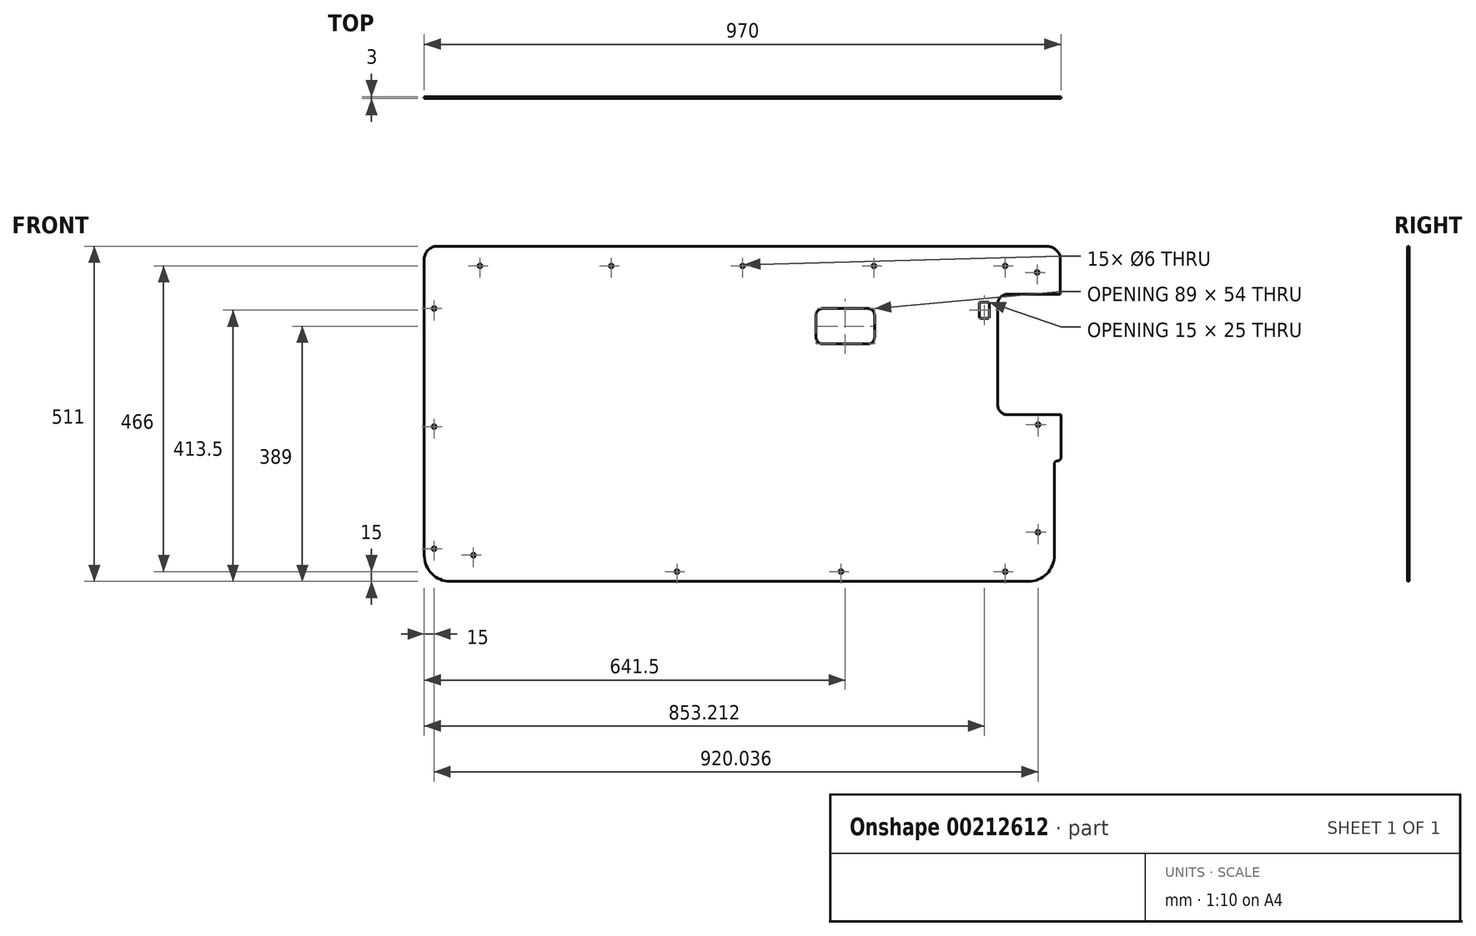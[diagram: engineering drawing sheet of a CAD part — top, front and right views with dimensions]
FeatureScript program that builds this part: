
annotation { "Feature Type Name" : "Feature", "Feature Type Description" : "" }
export const myFeature = defineFeature(function(context is Context, id is Id, definition is map)
    precondition{}
    {
        {
            var Q0;
            Q0=qCreatedBy(makeId("Front.planeOp"),FACE);
            var sketch = newSketch(context, id + "F0", { "sketchPlane" : qUnion([Q0])});
            skLineSegment(sketch, "E0.bottom", {"start": v(462.4, 255.5) * mm, "end": v(-465, 255.5) * mm});
            skLineSegment(sketch, "E0.top", {"start": v(435, -255.5) * mm, "end": v(435, -255.5) * mm});
            skLineSegment(sketch, "E0.right", {"start": v(-485, 235.5) * mm, "end": v(-485, -215.5) * mm});
            skPoint(sketch, "E0.middle", {"position": v(0, 0) * mm});
            skLineSegment(sketch, "E1", {"start": v(0, 509.33) * mm, "end": v(0, -613.63) * mm, "construction": true});
            skLineSegment(sketch, "E2", {"start": v(-633.66, 0) * mm, "end": v(624.03, 0) * mm, "construction": true});
            skPoint(sketch, "E2.endSnap0", {"position": v(457.9, 0) * mm});
            skPoint(sketch, "E3.visualSharp", {"position": v(-485, 255.5) * mm});
            skPoint(sketch, "E4.visualSharp", {"position": v(485, 255.5) * mm});
            skArc(sketch, "E4.filletArc", {"start": v(483.71, 240.43) * mm, "mid": v(475.46, 251.35) * mm, "end": v(462.4, 255.5) * mm});
            skPoint(sketch, "E5.visualSharp", {"position": v(-485, -255.5) * mm});
            skPoint(sketch, "E6.center.orphan", {"position": v(-400, 225.5) * mm});
            skArc(sketch, "E7.filletArc", {"start": v(-485, -215.5) * mm, "mid": v(-473.28, -243.78) * mm, "end": v(-445, -255.5) * mm});
            skArc(sketch, "E8.filletArc", {"start": v(-465, 255.5) * mm, "mid": v(-479.14, 249.64) * mm, "end": v(-485, 235.5) * mm});
            skLineSegment(sketch, "E9", {"start": v(457.9, 0) * mm, "end": v(457.9, 0) * mm});
            skLineSegment(sketch, "E10", {"start": v(483.71, 240.43) * mm, "end": v(483.71, 182.5) * mm});
            skLineSegment(sketch, "E11", {"start": v(388.71, 167.5) * mm, "end": v(388.71, 13.5) * mm});
            skLineSegment(sketch, "E12", {"start": v(112, 150.5) * mm, "end": v(112, 116.5) * mm});
            skLineSegment(sketch, "E13", {"start": v(122, 106.5) * mm, "end": v(191, 106.5) * mm});
            skLineSegment(sketch, "E14", {"start": v(201, 116.5) * mm, "end": v(201, 150.5) * mm});
            skLineSegment(sketch, "E15", {"start": v(122, 160.5) * mm, "end": v(191, 160.5) * mm});
            skPoint(sketch, "E16.visualSharp", {"position": v(112, 160.5) * mm});
            skArc(sketch, "E16.filletArc", {"start": v(122, 160.5) * mm, "mid": v(114.93, 157.57) * mm, "end": v(112, 150.5) * mm});
            skPoint(sketch, "E17.visualSharp", {"position": v(201, 160.5) * mm});
            skArc(sketch, "E17.filletArc", {"start": v(201, 150.5) * mm, "mid": v(198.07, 157.57) * mm, "end": v(191, 160.5) * mm});
            skPoint(sketch, "E18.visualSharp", {"position": v(201, 106.5) * mm});
            skArc(sketch, "E18.filletArc", {"start": v(191, 106.5) * mm, "mid": v(198.07, 109.43) * mm, "end": v(201, 116.5) * mm});
            skPoint(sketch, "E19.visualSharp", {"position": v(112, 106.5) * mm});
            skArc(sketch, "E19.filletArc", {"start": v(112, 116.5) * mm, "mid": v(114.93, 109.43) * mm, "end": v(122, 106.5) * mm});
            skLineSegment(sketch, "E20", {"start": v(360.71, 168.5) * mm, "end": v(360.71, 147.5) * mm});
            skLineSegment(sketch, "E21", {"start": v(362.71, 145.5) * mm, "end": v(373.71, 145.5) * mm});
            skLineSegment(sketch, "E22", {"start": v(375.71, 147.5) * mm, "end": v(375.71, 168.5) * mm});
            skLineSegment(sketch, "E23", {"start": v(373.71, 170.5) * mm, "end": v(362.71, 170.5) * mm});
            skPoint(sketch, "E24.visualSharp", {"position": v(360.71, 170.5) * mm});
            skArc(sketch, "E24.filletArc", {"start": v(362.71, 170.5) * mm, "mid": v(361.3, 169.91) * mm, "end": v(360.71, 168.5) * mm});
            skPoint(sketch, "E25.visualSharp", {"position": v(375.71, 170.5) * mm});
            skArc(sketch, "E25.filletArc", {"start": v(375.71, 168.5) * mm, "mid": v(375.13, 169.91) * mm, "end": v(373.71, 170.5) * mm});
            skPoint(sketch, "E26.visualSharp", {"position": v(375.71, 145.5) * mm});
            skArc(sketch, "E26.filletArc", {"start": v(373.71, 145.5) * mm, "mid": v(375.13, 146.09) * mm, "end": v(375.71, 147.5) * mm});
            skPoint(sketch, "E27.visualSharp", {"position": v(360.71, 145.5) * mm});
            skArc(sketch, "E27.filletArc", {"start": v(360.71, 147.5) * mm, "mid": v(361.3, 146.09) * mm, "end": v(362.71, 145.5) * mm});
            skPoint(sketch, "E28.center.orphan", {"position": v(-200, 225.5) * mm});
            skPoint(sketch, "E29.center.orphan", {"position": v(0, 225.5) * mm});
            skPoint(sketch, "E30.center.orphan", {"position": v(200, 225.5) * mm});
            skPoint(sketch, "E31.center.orphan", {"position": v(400, 225.5) * mm});
            skLineSegment(sketch, "E32", {"start": v(483.71, 182.5) * mm, "end": v(403.71, 182.5) * mm});
            skLineSegment(sketch, "E33", {"start": v(475, -215.5) * mm, "end": v(475, -81.5) * mm});
            skLineSegment(sketch, "E34", {"start": v(403.71, -1.5) * mm, "end": v(462.82, -1.5) * mm});
            skLineSegment(sketch, "E35", {"start": v(485, -1.5) * mm, "end": v(485, -61.5) * mm});
            skPoint(sketch, "E36.visualSharp", {"position": v(475, -71.5) * mm});
            skPoint(sketch, "E37.visualSharp", {"position": v(485, -1.5) * mm});
            skLineSegment(sketch, "E38", {"start": v(403.71, -1.5) * mm, "end": v(485, -1.5) * mm});
            skPoint(sketch, "E39.center.orphan", {"position": v(448.71, 215.5) * mm});
            skPoint(sketch, "E40.center.orphan", {"position": v(450, -16.5) * mm});
            skPoint(sketch, "E41.center.orphan", {"position": v(450, -180.5) * mm});
            skPoint(sketch, "E42.center.orphan", {"position": v(400, -240.5) * mm});
            skPoint(sketch, "E43.center.orphan", {"position": v(150, -240.5) * mm});
            skPoint(sketch, "E44.center.orphan", {"position": v(-100, -240.5) * mm});
            skPoint(sketch, "E45.center.orphan", {"position": v(-410, -215.5) * mm});
            skPoint(sketch, "E46.center.orphan", {"position": v(-470, -205.5) * mm});
            skPoint(sketch, "E47.center.orphan", {"position": v(-470, -19.5) * mm});
            skPoint(sketch, "E48.center.orphan", {"position": v(-470, 160.5) * mm});
            skPoint(sketch, "E49.visualSharp", {"position": v(388.71, 182.5) * mm});
            skArc(sketch, "E49.filletArc", {"start": v(403.71, 182.5) * mm, "mid": v(393.1, 178.1) * mm, "end": v(388.71, 167.5) * mm});
            skPoint(sketch, "E50.visualSharp", {"position": v(388.71, -1.5) * mm});
            skArc(sketch, "E50.filletArc", {"start": v(388.71, 13.5) * mm, "mid": v(393.1, 2.9) * mm, "end": v(403.71, -1.5) * mm});
            skLineSegment(sketch, "E51.trimOffspring", {"start": v(0, -255.5) * mm, "end": v(-445, -255.5) * mm});
            skPoint(sketch, "E52.visualSharp", {"position": v(475, -255.5) * mm});
            skArc(sketch, "E52.filletArc", {"start": v(435, -255.5) * mm, "mid": v(463.28, -243.78) * mm, "end": v(475, -215.5) * mm});
            skCircle(sketch, "E53", {"center": v(200.04, 225.5) * mm, "radius": 3 * mm});
            skPoint(sketch, "E54.center.orphan", {"position": v(399.93, 225.48) * mm});
            skCircle(sketch, "E55", {"center": v(399.97, 225.48) * mm, "radius": 3 * mm});
            skPoint(sketch, "E56.center.orphan", {"position": v(448.72, 215.5) * mm});
            skCircle(sketch, "E57", {"center": v(448.76, 215.5) * mm, "radius": 3 * mm});
            skCircle(sketch, "E58", {"center": v(450.04, -16.5) * mm, "radius": 3 * mm});
            skCircle(sketch, "E59", {"center": v(450, -180.5) * mm, "radius": 3 * mm});
            skCircle(sketch, "E60", {"center": v(400, -240.5) * mm, "radius": 3 * mm});
            skCircle(sketch, "E61", {"center": v(150, -240.5) * mm, "radius": 3 * mm});
            skCircle(sketch, "E62", {"center": v(-100, -240.5) * mm, "radius": 3 * mm});
            skCircle(sketch, "E63", {"center": v(-410, -215.5) * mm, "radius": 3 * mm});
            skCircle(sketch, "E64", {"center": v(-470, -205.5) * mm, "radius": 3 * mm});
            skCircle(sketch, "E65", {"center": v(-470, -19.5) * mm, "radius": 3 * mm});
            skCircle(sketch, "E66", {"center": v(-470, 160.5) * mm, "radius": 3 * mm});
            skCircle(sketch, "E67", {"center": v(-400, 225.5) * mm, "radius": 3 * mm});
            skCircle(sketch, "E68", {"center": v(-200, 225.5) * mm, "radius": 3 * mm});
            skCircle(sketch, "E69", {"center": v(0, 225.5) * mm, "radius": 3 * mm});
            skLineSegment(sketch, "E70", {"start": v(435, -255.5) * mm, "end": v(0, -255.5) * mm});
            skPoint(sketch, "E71.1.internal.orphan", {"position": v(480, -71.5) * mm});
            skPoint(sketch, "E71.startDerivative.orphan", {"position": v(485, -71.5) * mm});
            skLineSegment(sketch, "E72", {"start": v(480, -71.5) * mm, "end": v(480, -71.5) * mm});
            skLineSegment(sketch, "E73", {"start": v(475, -81.5) * mm, "end": v(475, -76.5) * mm});
            skArc(sketch, "E74.filletArc", {"start": v(480, -71.5) * mm, "mid": v(483.54, -70.04) * mm, "end": v(485, -66.5) * mm});
            skArc(sketch, "E75.filletArc", {"start": v(480, -71.5) * mm, "mid": v(476.46, -72.96) * mm, "end": v(475, -76.5) * mm});
            skLineSegment(sketch, "E76", {"start": v(485, -66.5) * mm, "end": v(485, -61.5) * mm});
            skSolve(sketch);
        }
        {
            var Q0;
            Q0=makeQuery(id+"F0.imprint","IMPRINT",FACE,{"disambiguationData":[TD([[makeQuery(id+"F0.imprint","IMPRINT",EDGE,{"derivedFrom":sQuery(id+"F0.wireOp",EDGE,"E0.bottom")}),1.0]])]});
            extrude(context, id + "F1", {"entities" : qUnion([Q0]), "depth" : 3 * mm, "symmetric" : true});
        }
    });
